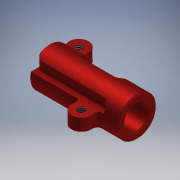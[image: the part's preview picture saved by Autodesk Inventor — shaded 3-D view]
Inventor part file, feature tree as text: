
AUTODESK INVENTOR PART (.ipt)
format: ipt  version: 2018 (Build 220112000, 112)  size: 369,664 bytes
history: native  units: mm
features: projected_geometry x8, extrude x7, sketch x7, thread x1, hole x1, fillet x1, chamfer x1
ambient origin geometry x8: Origin, YZ Plane, XZ Plane, XY Plane, X Axis, Y Axis, Z Axis, Center Point
bodies: Body1 (feature_tree)
feature tree (26):
  extrude  "Extrusion3"  Depth=15.0mm TaperAngle=0.0deg
  extrude  "Extrusion5"  Depth=10.0mm TaperAngle=0.0deg
  thread  "Thread2"  [1 undecoded]
  extrude  "Extrusion6"  Depth=1.05mm
  extrude  "Extrusion8"  Depth=8.0mm
  sketch  "Sketch11"  dims[d62=3.1mm d63=0.0mm d64=7.5mm]
  extrude  "Extrusion9"  Depth=7.5mm
  hole  "Hole2"  [1 undecoded]
  extrude  "Extrusion10"  Depth=1.0mm
  fillet  "Fillet5"  Radius=2.3mm
  chamfer  "Chamfer3"  Distance=4.8mm
  extrude  "Extrusion11"  Depth=1.0mm
  sketch  "Sketch4"  dims[d27=5.1mm d33=15.0mm d34=15.0mm d35=0.0mm d36=0.0mm]
  sketch  "Sketch7"  dims[d43=4.0mm d44=4.75mm d45=0.0mm d46=10.0mm d47=0.0mm]
  sketch  "Sketch8"  dims[d49=3.1mm d50=0.0mm d59=1.05mm]
  projected_geometry  "Projected Loop5"
  sketch  "Sketch10"  dims[d60=5.5mm d61=8.0mm]
  projected_geometry  "Projected Loop7"
  projected_geometry  "Projected Loop8"
  projected_geometry  "Projected Loop9"
  sketch  "Sketch12"  dims[d65=5.6mm d66=2.3mm]
  projected_geometry  "Projected Loop10"
  projected_geometry  "Projected Loop11"
  sketch  "Sketch13"  dims[d67=0.5mm d68=0.2mm d71=2.3mm d72=4.8mm d73=2.0mm d74=5.5mm d75=5.5mm d76=2.5mm d77=0.0mm d78=1.567mm d79=4.0mm d80=4.0mm d81=2.0mm d82=90.0deg d83=6.3mm d84=20.594885mm d85=8.4mm d86=1.0mm d87=2.45mm d88=1.25mm d89=0.0mm d90=0.0mm d91=3.0mm d92=1.0mm d93=0.5mm d94=0.5mm d95=3.0mm d96=0.25mm d97=2.0mm d98=45.0deg d99=2.45mm d100=0.0mm]
  projected_geometry  "Projected Loop12"
  projected_geometry  "Projected Loop13"
note: 2 required parameter values undecoded (feature->parameter linkage not recoverable at this tier; creation-order binding heuristic only, values carry confidence <= 0.55)
